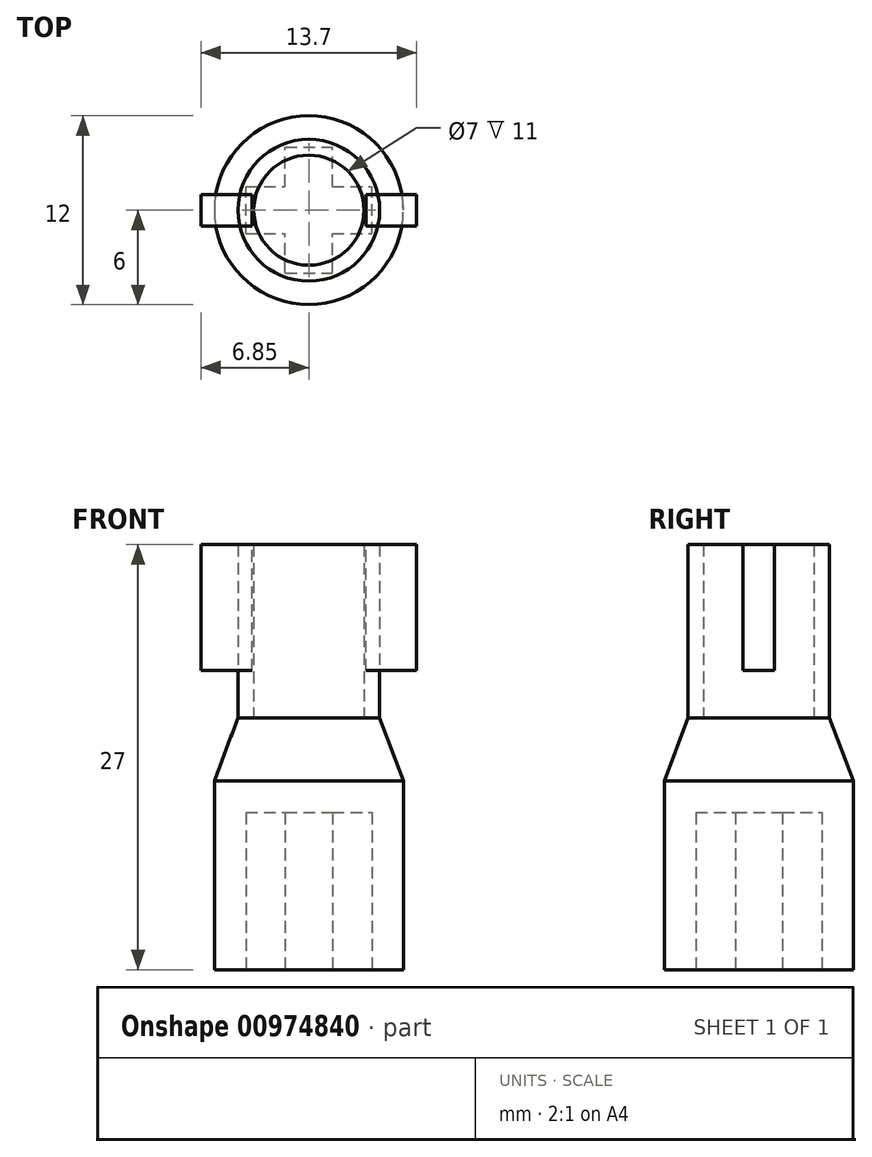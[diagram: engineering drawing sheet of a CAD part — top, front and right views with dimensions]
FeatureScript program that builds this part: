
annotation { "Feature Type Name" : "Feature", "Feature Type Description" : "" }
export const myFeature = defineFeature(function(context is Context, id is Id, definition is map)
    precondition{}
    {
        {
            var Q0;
            Q0=qCreatedBy(makeId("Top.planeOp"),FACE);
            var sketch = newSketch(context, id + "F0", { "sketchPlane" : qUnion([Q0])});
            skCircle(sketch, "E0", {"center": v(0, 0) * mm, "radius": 4.5 * mm});
            skCircle(sketch, "E1", {"center": v(0, 0) * mm, "radius": 3.5 * mm});
            skSolve(sketch);
        }
        {
            var Q0;
            Q0=qSketchRegion(id+"F0",true);
            extrude(context, id + "F1", {"entities" : qUnion([Q0]), "depth" : 11 * mm, "offsetDistance" : 25 * mm});
        }
        {
            var Q0;
            Q0=makeQuery(id+"F1.opExtrude","CAP_FACE",FACE,{"disambiguationData":[OSD([sQuery(id+"F0.wireOp",EDGE,"E0"),sQuery(id+"F0.wireOp",EDGE,"E1")])],"isStart":false});
            var sketch = newSketch(context, id + "F2", { "sketchPlane" : qUnion([Q0])});
            skLineSegment(sketch, "E2", {"start": v(-6.85, -1) * mm, "end": v(-3.62, -1) * mm});
            skLineSegment(sketch, "E3", {"start": v(6.85, 1) * mm, "end": v(3.62, 1) * mm});
            skLineSegment(sketch, "E4", {"start": v(-6.85, 1) * mm, "end": v(-6.85, -1) * mm});
            skLineSegment(sketch, "E5", {"start": v(6.85, 1) * mm, "end": v(6.85, -1) * mm});
            skLineSegment(sketch, "E6.trimOffspring", {"start": v(-3.62, 1) * mm, "end": v(-6.85, 1) * mm});
            skLineSegment(sketch, "E7.trimOffspring", {"start": v(3.62, -1) * mm, "end": v(6.85, -1) * mm});
            skPoint(sketch, "E8.center.orphan", {"position": v(0, 0) * mm});
            skLineSegment(sketch, "E9", {"start": v(-3.62, 1) * mm, "end": v(-3.62, -1) * mm});
            skLineSegment(sketch, "E10", {"start": v(3.62, 1) * mm, "end": v(3.62, -1) * mm});
            skSolve(sketch);
        }
        {
            var Q0;
            Q0=qSketchRegion(id+"F2",true);
            extrude(context, id + "F3", {"entities" : qUnion([Q0]), "oppositeDirection" : true, "depth" : 8 * mm, "offsetDistance" : 25 * mm});
        }
        {
            var Q0;
            Q0=makeQuery(id+"F1.opExtrude","CAP_FACE",FACE,{"disambiguationData":[OSD([sQuery(id+"F0.wireOp",EDGE,"E0"),sQuery(id+"F0.wireOp",EDGE,"E1")])],"isStart":true});
            var sketch = newSketch(context, id + "F4", { "sketchPlane" : qUnion([Q0])});
            skCircle(sketch, "E11", {"center": v(0, 0) * mm, "radius": 6 * mm});
            skSolve(sketch);
        }
        {
            var Q0;
            Q0 = qSketchRegion(id + "F4", true);
            extrude(context, id + "F5", {"entities" : qUnion([Q0]), "operationType" : NewBodyOperationType.ADD, "depth" : 16 * mm, "offsetDistance" : 25 * mm});
        }
        {
            var Q0;
            Q0=makeQuery(id+"F5.opExtrude","CAP_EDGE",EDGE,{"disambiguationData":[OSD([sQuery(id+"F4.wireOp",EDGE,"E11")])],"isStart":true});
            chamfer(context, id + "F6", {"entities" : qUnion([Q0]), "chamferType" : ChamferType.TWO_OFFSETS, "width1" : 4 * mm, "oppositeDirection" : false, "width2" : 1.5 * mm, "tangentPropagation" : true});
        }
        {
            var Q0;
            Q0=makeQuery(id+"F5.opExtrude","CAP_FACE",FACE,{"disambiguationData":[OSD([sQuery(id+"F4.wireOp",EDGE,"E11")])],"isStart":false});
            var sketch = newSketch(context, id + "F7", { "sketchPlane" : qUnion([Q0])});
            skLineSegment(sketch, "E12.bottom", {"start": v(-4, 1.5) * mm, "end": v(-1.5, 1.5) * mm});
            skLineSegment(sketch, "E12.top", {"start": v(-4, -1.5) * mm, "end": v(-1.5, -1.5) * mm});
            skLineSegment(sketch, "E12.left", {"start": v(-4, 1.5) * mm, "end": v(-4, -1.5) * mm});
            skLineSegment(sketch, "E12.right", {"start": v(4, 1.5) * mm, "end": v(4, -1.5) * mm});
            skPoint(sketch, "E12.middle", {"position": v(0, 0) * mm});
            skLineSegment(sketch, "E13.bottom", {"start": v(-1.5, 4) * mm, "end": v(1.5, 4) * mm});
            skLineSegment(sketch, "E13.top", {"start": v(-1.5, -4) * mm, "end": v(1.5, -4) * mm});
            skLineSegment(sketch, "E13.left", {"start": v(-1.5, 4) * mm, "end": v(-1.5, 1.5) * mm});
            skLineSegment(sketch, "E13.right", {"start": v(1.5, 4) * mm, "end": v(1.5, 1.5) * mm});
            skLineSegment(sketch, "E14.trimOffspring", {"start": v(1.5, -1.5) * mm, "end": v(1.5, -4) * mm});
            skLineSegment(sketch, "E15.trimOffspring", {"start": v(1.5, 1.5) * mm, "end": v(4, 1.5) * mm});
            skLineSegment(sketch, "E16.trimOffspring", {"start": v(-1.5, -1.5) * mm, "end": v(-1.5, -4) * mm});
            skLineSegment(sketch, "E17.trimOffspring", {"start": v(1.5, -1.5) * mm, "end": v(4, -1.5) * mm});
            skSolve(sketch);
        }
        {
            var Q0;
            Q0 = qSketchRegion(id + "F7", true);
            extrude(context, id + "F8", {"entities" : qUnion([Q0]), "operationType" : NewBodyOperationType.REMOVE, "oppositeDirection" : true, "depth" : 10 * mm, "offsetDistance" : 25 * mm});
        }
    });
